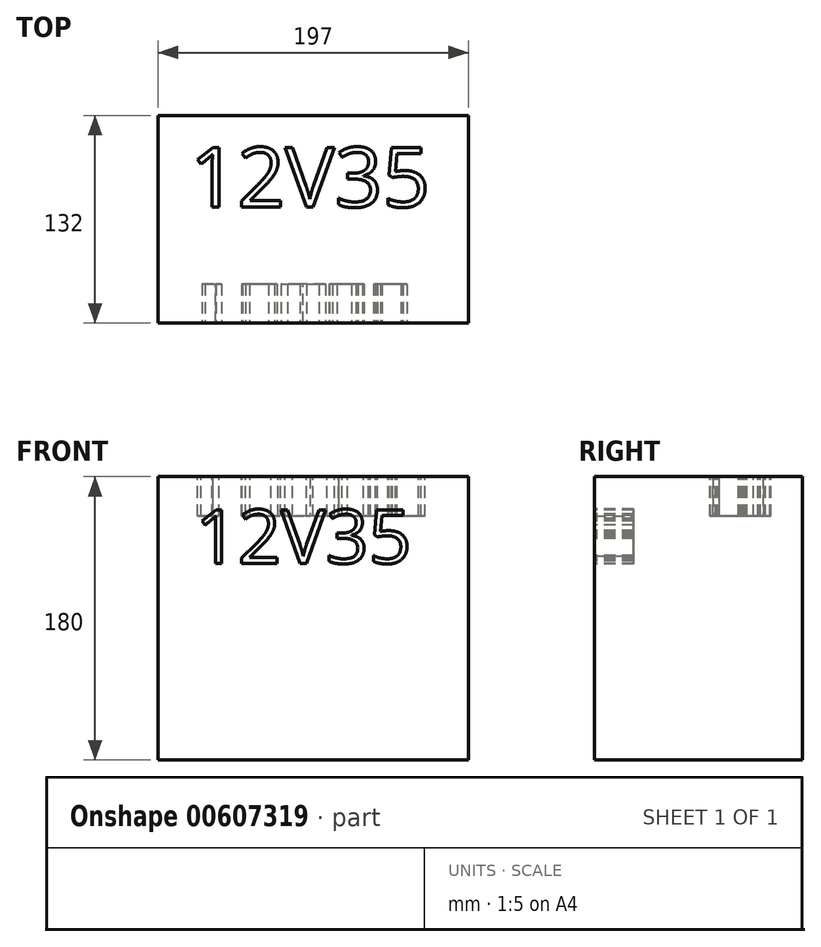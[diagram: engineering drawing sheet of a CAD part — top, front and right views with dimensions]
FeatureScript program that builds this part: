
annotation { "Feature Type Name" : "Feature", "Feature Type Description" : "" }
export const myFeature = defineFeature(function(context is Context, id is Id, definition is map)
    precondition{}
    {
        {
            var Q0;
            Q0=qCreatedBy(makeId("Top.planeOp"),FACE);
            var sketch = newSketch(context, id + "F0", { "sketchPlane" : qUnion([Q0])});
            skLineSegment(sketch, "E0.bottom", {"start": v(0, 0) * mm, "end": v(197, 0) * mm});
            skLineSegment(sketch, "E0.top", {"start": v(0, 132) * mm, "end": v(197, 132) * mm});
            skLineSegment(sketch, "E0.left", {"start": v(0, 0) * mm, "end": v(0, 132) * mm});
            skLineSegment(sketch, "E0.right", {"start": v(197, 0) * mm, "end": v(197, 132) * mm});
            skSolve(sketch);
        }
        {
            var Q0;
            Q0 = qSketchRegion(id + "F0", true);
            extrude(context, id + "F1", {"entities" : qUnion([Q0]), "depth" : 180 * mm, "offsetDistance" : 25 * mm});
        }
        {
            var Q0;
            Q0=makeQuery(id+"F1.opExtrude","CAP_FACE",FACE,{"disambiguationData":[OSD([sQuery(id+"F0.wireOp",EDGE,"E0.bottom"),sQuery(id+"F0.wireOp",EDGE,"E0.top"),sQuery(id+"F0.wireOp",EDGE,"E0.left"),sQuery(id+"F0.wireOp",EDGE,"E0.right")])],"isStart":false});
            var sketch = newSketch(context, id + "F2", { "sketchPlane" : qUnion([Q0])});
            skText(sketch, "E1", { "text": "12V35\n", "fontName": "OpenSans-Regular.ttf"});
            const initialGuessF2  = {"E1": [0.02, 0.07387, 1, 0, 0.03813]};
            skSetInitialGuess(sketch, initialGuessF2);
            skSolve(sketch);
        }
        {
            var Q0;
            Q0 = qSketchRegion(id + "F2", true);
            extrude(context, id + "F3", {"entities" : qUnion([Q0]), "operationType" : NewBodyOperationType.REMOVE, "oppositeDirection" : true, "depth" : 25 * mm, "offsetDistance" : 25 * mm});
        }
        {
            var Q0;
            Q0=makeQuery(id+"F1.opExtrude","SWEPT_FACE",FACE,{"disambiguationData":[OSD([sQuery(id+"F0.wireOp",EDGE,"E0.bottom")])]});
            var sketch = newSketch(context, id + "F4", { "sketchPlane" : qUnion([Q0])});
            skText(sketch, "E2", { "text": "12V35\n", "fontName": "OpenSans-Regular.ttf"});
            const initialGuessF4  = {"E2": [0.02347, 0.125, 1, 0, 0.0343]};
            skSetInitialGuess(sketch, initialGuessF4);
            skSolve(sketch);
        }
        {
            var Q0;
            Q0 = qSketchRegion(id + "F4", true);
            extrude(context, id + "F5", {"entities" : qUnion([Q0]), "operationType" : NewBodyOperationType.REMOVE, "oppositeDirection" : true, "depth" : 25 * mm, "offsetDistance" : 25 * mm});
        }
    });
